# Revit family: QF_ZANUSSI_392332_Z9KKGABAMEA
name_source: partatom
category: Specialty Equipment
revit_build: Autodesk Revit 2018 (Build: 20190510_1515(x64)
units: mm (PartAtom-declared; Revit-internal decimal feet)

## family parameters
Always vertical = Yes
Cut with Voids When Loaded = No
Part Type = Normal
Room Calculation Point = No
Round Connector Dimension = Use Diameter
Shared = No
Work Plane-Based = No

## types (1)
- QF_ZANUSSI_392332_Z9KKGABAMEA
    Accessory = Yes
    Apparent Power = 36000 VA
    Cold Water Size = 0"
    Compressed Air Pressure = 0.00 psi
    Compressed Air Size = 0"
    Compressed Air Volume = 0 GPM
    Condensate Return Size = 0"
    Conn Conduit = Yes
    Depth = 915 mm  [stored 3.00197 ft]
    Depth Actual = 900 mm  [stored 2.95276 ft]
    Description = 23+23LT GAS FRYER-2 WELLS+4 1/2 BASKETS
    Direct Waste Size = 0"
    FL Amps = 52 A
    Gas Input = 1.3 Btu/h
    Gas KW = 42
    Gas Size = 1"
    HP = 0 HP
    Height = 851 mm  [stored 2.79199 ft]
    Height Actual = 850 mm  [stored 2.78871 ft]
    Hot Water Size = 0"
    Length Actual = 800 mm  [stored 2.62467 ft]
    Manufacturer = Zanussi
    Max Overcurrent Protection = 0 A
    Min Ckt Ampacity = 0 A
    Model = Z9KKGABAMEA
    Phase = 3
    Refrigerant Compressor Remote = Yes
    Refrigeration Liquid Line Size = 0"
    Refrigeration Suction Line Size = 0"
    Steam Pounds per Hour = 0
    Steam Supply Maximum Pressure = 0.00 psi
    Steam Supply Minimum Pressure = 0.00 psi
    Steam Supply Size = 0"
    URL = http://www.zanussiprofessional.com
    URL Cutsheet = www.electrolux.com/foodservice
    URL Manufacturer = http://www.zanussiprofessional.com
    Volts = 400 V
    Watts = 36000 W
    Weight = 0.00 kg
    Weight in Pounds = 115
    Width = 800 mm  [stored 2.62467 ft]

note: [stored X ft] marks values corroborated as IEEE doubles in the binary element streams (Revit-internal decimal feet)

## geometry (parser evidence)
native form markers: Blend x16, Sweep x3
no freeform markers — native parametric forms only
